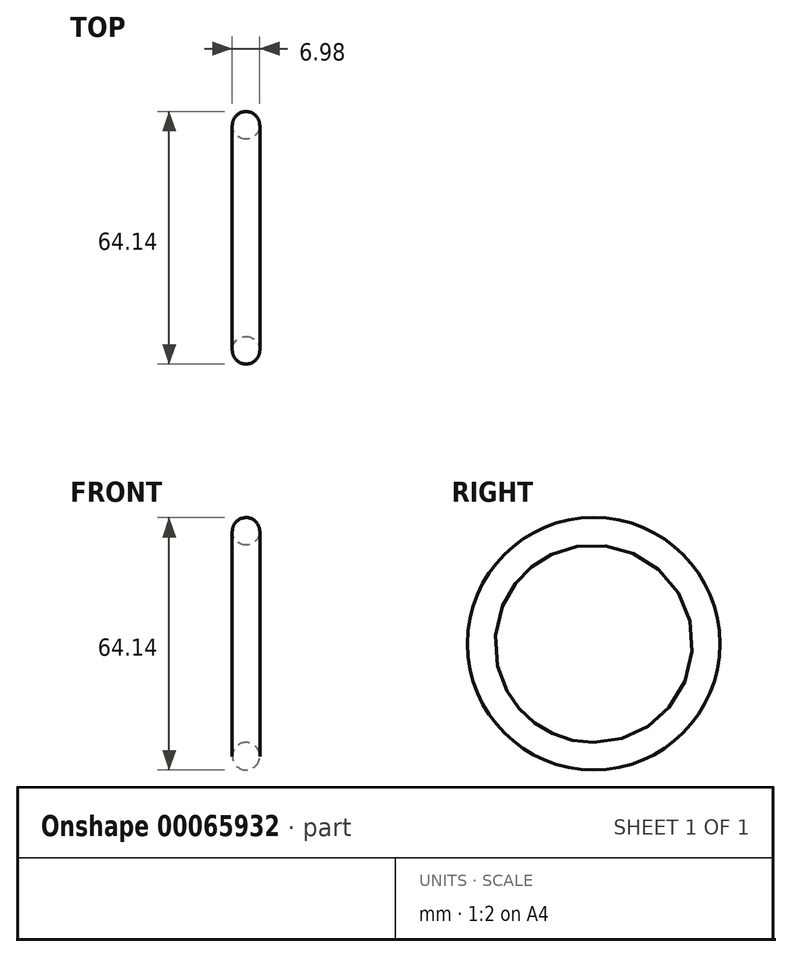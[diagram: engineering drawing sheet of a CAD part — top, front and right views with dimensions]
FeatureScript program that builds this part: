
annotation { "Feature Type Name" : "Feature", "Feature Type Description" : "" }
export const myFeature = defineFeature(function(context is Context, id is Id, definition is map)
    precondition{}
    {
        {
            var Q0;
            Q0=qCreatedBy(makeId("Front.planeOp"),FACE);
            var sketch = newSketch(context, id + "F0", { "sketchPlane" : qUnion([Q0])});
            skLineSegment(sketch, "E0", {"start": v(0, 0) * mm, "end": v(-6.06, 0) * mm, "construction": true});
            skCircle(sketch, "E1", {"center": v(0, 28.58) * mm, "radius": 3.5 * mm});
            skSolve(sketch);
        }
        {
            var Q0;
            Q0=makeQuery(id+"F0.imprint","IMPRINT",FACE,{"disambiguationData":[TD([[makeQuery(id+"F0.imprint","IMPRINT",EDGE,{"derivedFrom":sQuery(id+"F0.wireOp",EDGE,"E1")}),1.0]])]});
            var Q1;
            Q1=sQuery(id+"F0.wireOp",EDGE,"E0");
            revolve(context, id + "F1", {"entities" : qUnion([Q0]), "axis" : qUnion([Q1]), "revolveType" : RevolveType.FULL});
        }
    });
